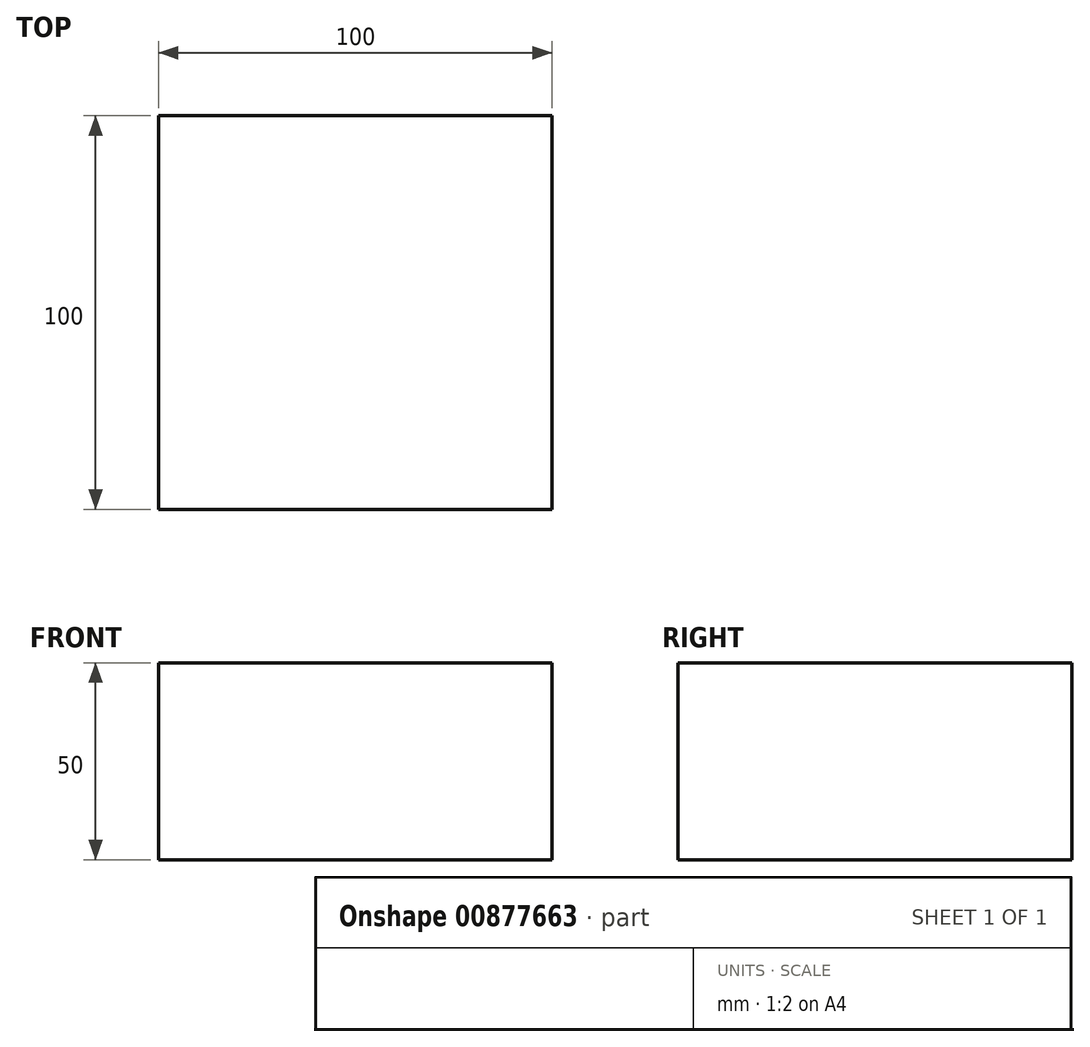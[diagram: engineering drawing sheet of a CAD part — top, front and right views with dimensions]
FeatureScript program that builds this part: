
annotation { "Feature Type Name" : "Feature", "Feature Type Description" : "" }
export const myFeature = defineFeature(function(context is Context, id is Id, definition is map)
    precondition{}
    {
        {
            var Q0;
            Q0=qCreatedBy(makeId("Top.planeOp"),FACE);
            var sketch = newSketch(context, id + "F0", { "sketchPlane" : qUnion([Q0])});
            skLineSegment(sketch, "E0.bottom", {"start": v(50, 50) * mm, "end": v(-50, 50) * mm});
            skLineSegment(sketch, "E0.top", {"start": v(50, -50) * mm, "end": v(-50, -50) * mm});
            skLineSegment(sketch, "E0.left", {"start": v(50, 50) * mm, "end": v(50, -50) * mm});
            skLineSegment(sketch, "E0.right", {"start": v(-50, 50) * mm, "end": v(-50, -50) * mm});
            skPoint(sketch, "E0.middle", {"position": v(0, 0) * mm});
            skSolve(sketch);
        }
        {
            var Q0;
            Q0=makeQuery(id+"F0.imprint","IMPRINT",FACE,{"disambiguationData":[TD([[makeQuery(id+"F0.imprint","IMPRINT",EDGE,{"derivedFrom":sQuery(id+"F0.wireOp",EDGE,"E0.bottom")}),1.0]])]});
            extrude(context, id + "F1", {"entities" : qUnion([Q0]), "depth" : 50 * mm, "offsetDistance" : 25 * mm});
        }
    });
